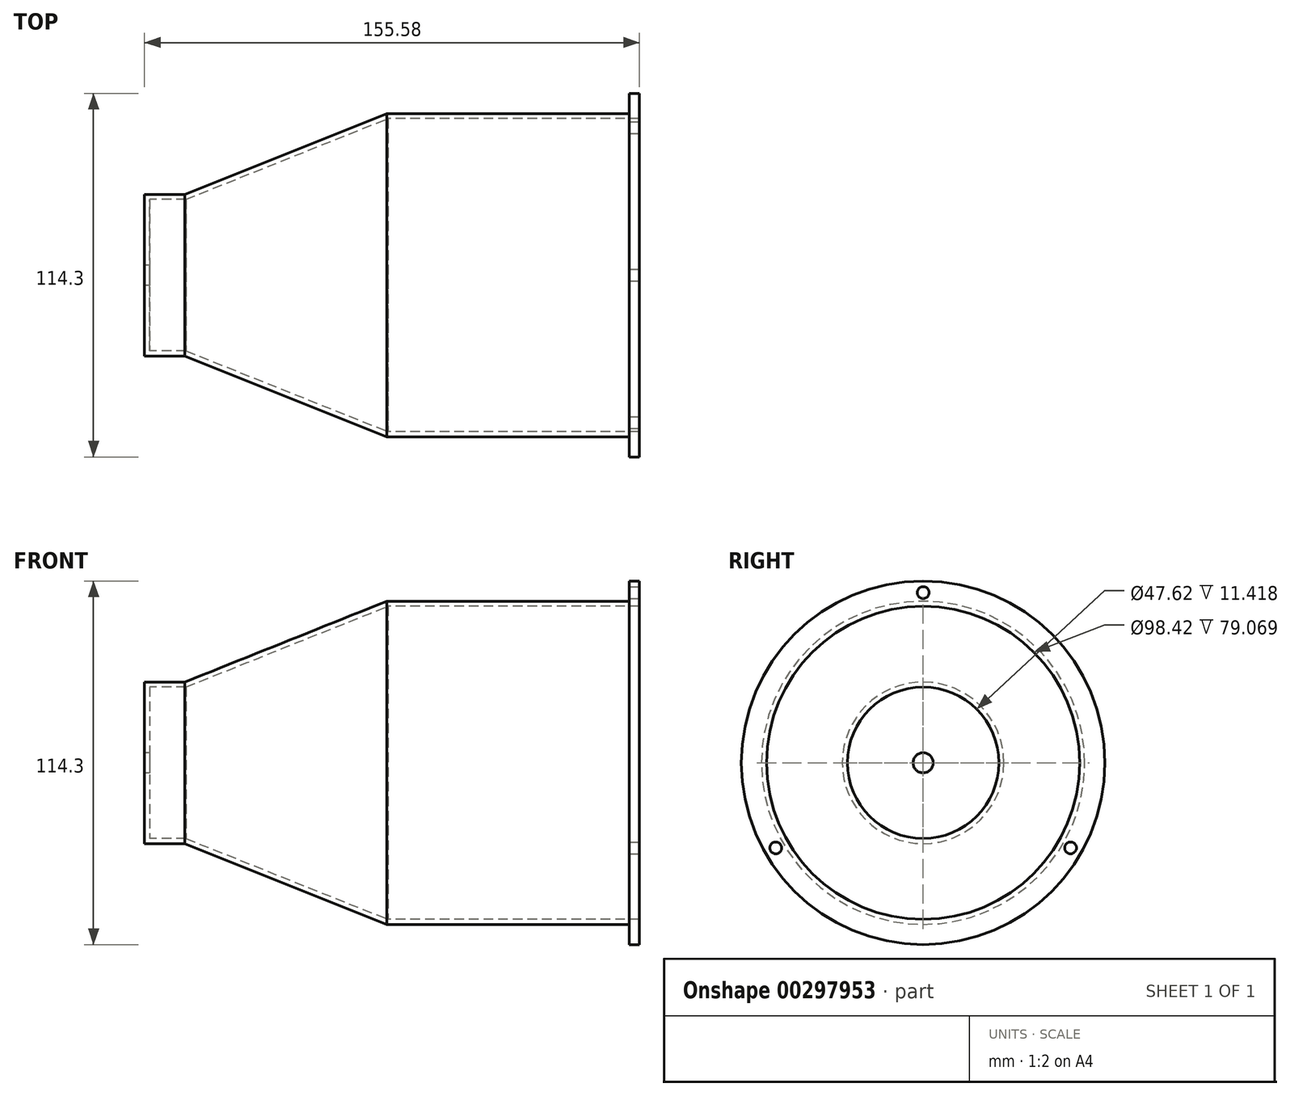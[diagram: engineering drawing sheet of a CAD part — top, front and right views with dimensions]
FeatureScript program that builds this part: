
annotation { "Feature Type Name" : "Feature", "Feature Type Description" : "" }
export const myFeature = defineFeature(function(context is Context, id is Id, definition is map)
    precondition{}
    {
        {
            var Q0;
            Q0=qCreatedBy(makeId("Front.planeOp"),FACE);
            var sketch = newSketch(context, id + "F0", { "sketchPlane" : qUnion([Q0])});
            skLineSegment(sketch, "E0.top", {"start": v(76.2, 50.8) * mm, "end": v(152.4, 50.8) * mm});
            skLineSegment(sketch, "E1.top", {"start": v(0, 25.4) * mm, "end": v(12.7, 25.4) * mm});
            skLineSegment(sketch, "E1.left", {"start": v(0, 3.18) * mm, "end": v(0, 25.4) * mm});
            skLineSegment(sketch, "E2", {"start": v(12.7, 25.4) * mm, "end": v(76.2, 50.8) * mm});
            skLineSegment(sketch, "E3", {"start": v(0, 0) * mm, "end": v(152.4, 0) * mm, "construction": true});
            skLineSegment(sketch, "E4.0", {"start": v(1.59, 23.81) * mm, "end": v(13, 23.81) * mm});
            skLineSegment(sketch, "E4.1", {"start": v(1.59, 3.18) * mm, "end": v(1.59, 23.81) * mm});
            skLineSegment(sketch, "E5.0", {"start": v(76.5, 49.21) * mm, "end": v(152.4, 49.21) * mm});
            skLineSegment(sketch, "E5.1", {"start": v(13, 23.81) * mm, "end": v(76.5, 49.21) * mm});
            skLineSegment(sketch, "E6", {"start": v(152.4, 50.8) * mm, "end": v(152.4, 49.21) * mm});
            skLineSegment(sketch, "E7", {"start": v(0, 3.18) * mm, "end": v(1.59, 3.18) * mm});
            skSolve(sketch);
        }
        {
            var Q0;
            Q0=makeQuery(id+"F0.imprint","IMPRINT",FACE,{"disambiguationData":[TD([[makeQuery(id+"F0.imprint","IMPRINT",EDGE,{"derivedFrom":sQuery(id+"F0.wireOp",EDGE,"E0.top")}),-1.0]])]});
            var Q1;
            Q1=sQuery(id+"F0.wireOp",EDGE,"E3");
            revolve(context, id + "F1", {"entities" : qUnion([Q0]), "axis" : qUnion([Q1]), "revolveType" : RevolveType.FULL});
        }
        {
            var Q0;
            Q0=makeQuery(id+"F1.opRevolve","SWEPT_FACE",FACE,{"disambiguationData":[OSD([sQuery(id+"F0.wireOp",EDGE,"E6")])]});
            var sketch = newSketch(context, id + "F2", { "sketchPlane" : qUnion([Q0])});
            skCircle(sketch, "E8.0", {"center": v(0, 0) * mm, "radius": 57.15 * mm});
            skCircle(sketch, "E9.0", {"center": v(0, 0) * mm, "radius": 49.21 * mm});
            skSolve(sketch);
        }
        {
            var Q0;
            Q0 = qSketchRegion(id + "F2", true);
            extrude(context, id + "F3", {"entities" : qUnion([Q0]), "operationType" : NewBodyOperationType.ADD, "depth" : 3.17 * mm});
        }
        {
            var Q0;
            Q0=makeQuery(id+"F3.opExtrude","CAP_FACE",FACE,{"disambiguationData":[OSD([sQuery(id+"F2.wireOp",EDGE,"E8.0"),sQuery(id+"F2.wireOp",EDGE,"E9.0")])],"isStart":false});
            var sketch = newSketch(context, id + "F4", { "sketchPlane" : qUnion([Q0])});
            skCircle(sketch, "E10", {"center": v(0, 53.5) * mm, "radius": 1.86 * mm});
            skCircle(sketch, "E11.1.0", {"center": v(-46.33, -26.75) * mm, "radius": 1.86 * mm});
            skCircle(sketch, "E11.2.0", {"center": v(46.33, -26.75) * mm, "radius": 1.86 * mm});
            skPoint(sketch, "E11.center", {"position": v(0, 0) * mm});
            skSolve(sketch);
        }
        {
            var Q0;
            Q0=makeQuery(id+"F4.imprint","IMPRINT",FACE,{"disambiguationData":[TD([[makeQuery(id+"F4.imprint","IMPRINT",EDGE,{"derivedFrom":sQuery(id+"F4.wireOp",EDGE,"E10")}),1.0]])]});
            var Q1;
            Q1=makeQuery(id+"F4.imprint","IMPRINT",FACE,{"disambiguationData":[TD([[makeQuery(id+"F4.imprint","IMPRINT",EDGE,{"derivedFrom":sQuery(id+"F4.wireOp",EDGE,"E11.2.0")}),1.0]])]});
            var Q2;
            Q2=makeQuery(id+"F4.imprint","IMPRINT",FACE,{"disambiguationData":[TD([[makeQuery(id+"F4.imprint","IMPRINT",EDGE,{"derivedFrom":sQuery(id+"F4.wireOp",EDGE,"E11.1.0")}),1.0]])]});
            extrude(context, id + "F5", {"entities" : qUnion([Q0, Q1, Q2]), "operationType" : NewBodyOperationType.REMOVE, "endBound" : BoundingType.THROUGH_ALL, "oppositeDirection" : true, "depth" : 25.4 * mm});
        }
    });
